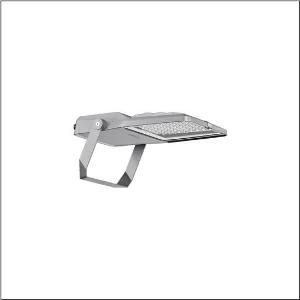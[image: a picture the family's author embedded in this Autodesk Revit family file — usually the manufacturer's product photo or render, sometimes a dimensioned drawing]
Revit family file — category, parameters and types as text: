
# Revit family: floodlight_fl_21_iq_mini___pl64_5xa7771c2e1a_63e9
name_source: partatom
category: Lighting Fixtures
units: mm (PartAtom-declared; Revit-internal decimal feet)

## family parameters
Cut with Voids When Loaded = No
Host = Face
Light Source = No
Part Type = Normal
Room Calculation Point = No
Round Connector Dimension = Use Diameter
Shared = No

## types (1)
- --- (1 x LED, 11790 lm, 87.2 W, 3000K)
    Apparent Load = 87 VA
    CIE Flux Codes = 28 80 98 100 100
    Color Rendering = 70
    Color Temperature = 3000K
    Default Elevation = 1800 mm
    Description = Floodlight FL 21 iQ mini, floodlight, primary light control with lens, of PMMA, primary optical cover: protective disc, of toughened safety glass, transparent, light distribution: PL64, light emission: direct distribution, installation type: surface-mounted, lamps: LED, High Power LED, rated values: 11.790lm | 87,2W | 135,2lm/W (begin service life); end service life: 11.790lm | 92,1W; at 50% lumin. flux: 5.895lm | 40,1W | 147lm/W, colour temperature: 3000K, colour rendering: CRI > 70, light colour: 730, light setting 1 begin service life: 100% | 11.790lm | 87,2W | 135,2lm/W | 3.000K, light setting 1 end service life: 92,1W, further light settings possible, control: Auto-Match, Temp-Guard, Lumen-Switch, Night-Set, Smart-Wire, Light-Fading, Desk-Remote (wireless, voltage-free reading and setting of iQ features in the workshop via application-optimized NFC function/RFID function), optimised constant luminous flux control (CLO 2.0), pre-setting: linear dimming characteristic, with terminal, 6-pole, mains connection: 220..240V, AC, 50/60Hz, luminaire housing, of diecast aluminium, powder-coated, SITECO metallic grey (DB 702S), corrosivity category C5 mid according to DIN EN ISO 12944suitable for swimming poolschlorine-resistant, sealing non-destructively replaceable, mounting bracket, of steel, galvanised, powder-coated, SITECO metallic grey (DB 702S), protection rating (complete): IP66, insulation class (complete): insulation class II (safety insulation), certification: CE, ENEC, VDE, protection symbol: D, impact resistance: IK08, permissible operating ambient temperature: -40..+40°C, permissible operating ambient temperature for outdoor applications: -40..+50°C, standard: DIN EN 12944, LABS conformity tested according to VDMA 24364:2018-05, packaging unit: 1 piece

Light Distribution: PL64
    Height = 70 mm
    Lamp = 1 x LED
    Lamp Light Flux = 11790 lm
    Lamp Power = 87.2 W
    Lamp count = 1
    Length = 485 mm
    Luminous efficacy = 135 lm/W
    Manufacturer = Siteco
    ModVariant = No
    Model = 5XA7771C2E1A
    Mounting Place = Pole
    Mounting Type = Pole annexe
    Number of Poles = 1
    OnlyDefault = Yes
    Power Factor = 1
    Product Name = Floodlight FL 21 iQ mini | PL64
    Product group = floodlight | pylon annexe
    ProductGroupID = 6201
    Protection Class = Protection class II
    Protection Degree = IP 66
    RLX_Detail_Level = 1
    RLX_Emergency_Light_Flux = 0 lm
    RLX_Emergency_Type = 0
    RLX_Emergency_Type_DB = No
    RlxData = <blob elided: 96625 chars, md5=14163cff>
    Socket = socket
    Standby Power = 0 W
    System Light Flux = 11790 lm
    System Power = 87 W
    Type Comments = factory setting: luminous flux: 100 % | dim-lin: 254 | 456 mA
    Type Image = l_1006845.jpg
    URL = http://relux.com
    VarID = @adj_167719
    Voltage = 0 V
    Weight = 0.00 kg
    Width = 337 mm

## geometry (parser evidence)
native form markers: Blend x4, Sweep x12
no freeform markers — native parametric forms only
